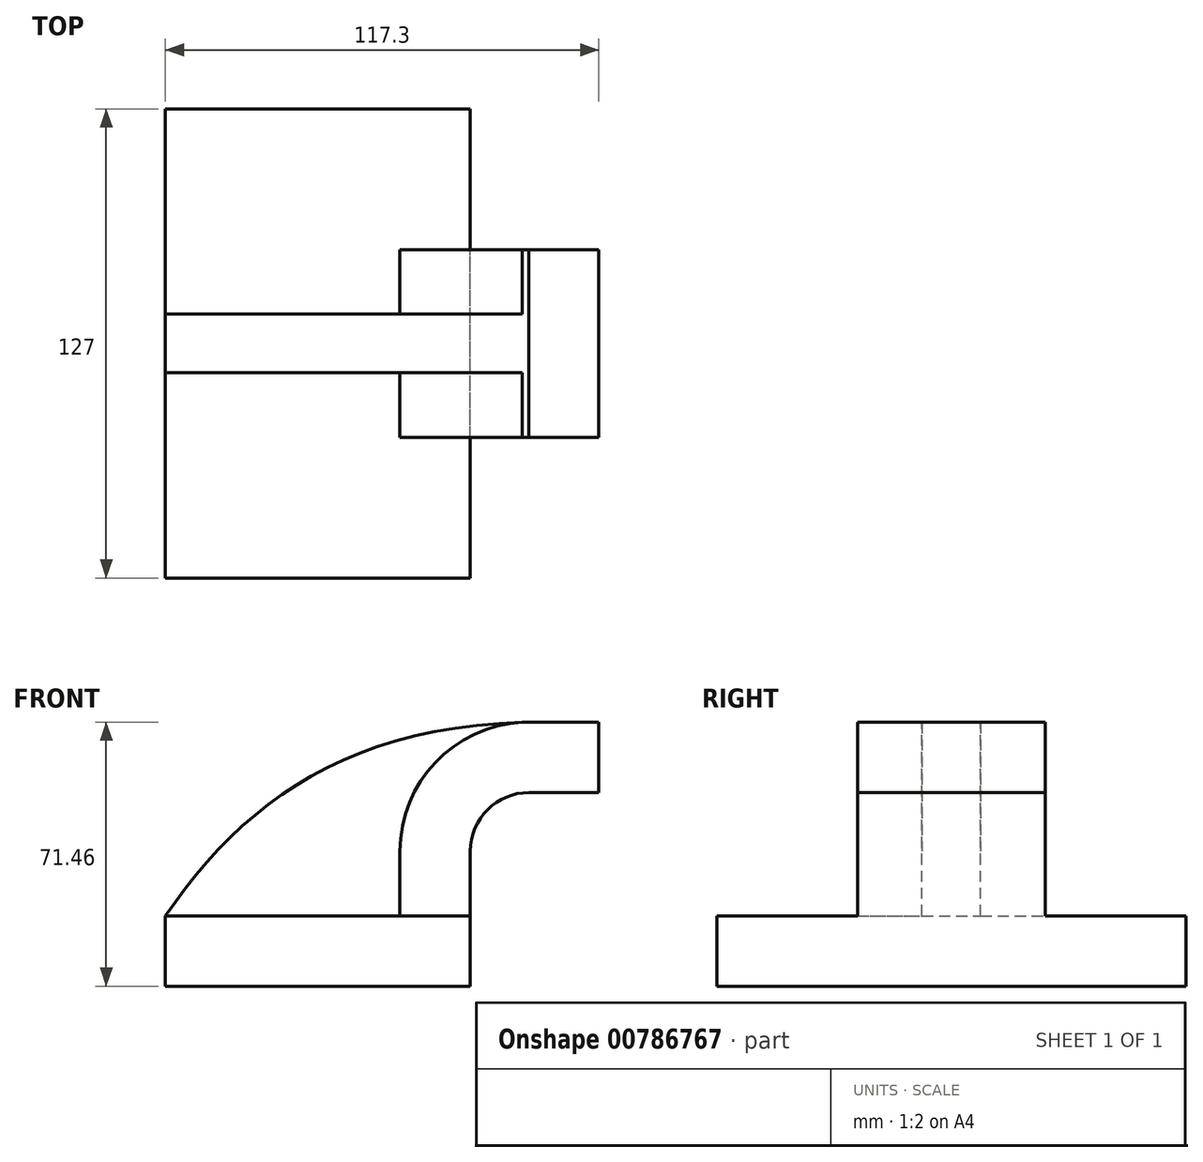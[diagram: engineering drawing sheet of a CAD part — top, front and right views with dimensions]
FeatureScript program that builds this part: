
annotation { "Feature Type Name" : "Feature", "Feature Type Description" : "" }
export const myFeature = defineFeature(function(context is Context, id is Id, definition is map)
    precondition{}
    {
        {
            var Q0;
            Q0=qCreatedBy(makeId("Front.planeOp"),FACE);
            var sketch = newSketch(context, id + "F0", { "sketchPlane" : qUnion([Q0])});
            skLineSegment(sketch, "E0.bottom", {"start": v(41.28, -9.52) * mm, "end": v(-41.28, -9.53) * mm});
            skLineSegment(sketch, "E0.top", {"start": v(41.27, 9.53) * mm, "end": v(-41.28, 9.53) * mm});
            skLineSegment(sketch, "E0.left", {"start": v(41.28, -9.52) * mm, "end": v(41.28, 9.53) * mm});
            skLineSegment(sketch, "E0.right", {"start": v(-41.28, -9.52) * mm, "end": v(-41.28, 9.53) * mm});
            skPoint(sketch, "E0.middle", {"position": v(0, 0) * mm});
            skLineSegment(sketch, "E1.bottom", {"start": v(111.12, 38.1) * mm, "end": v(60.32, 38.1) * mm});
            skLineSegment(sketch, "E1.top", {"start": v(111.12, 66.68) * mm, "end": v(60.32, 66.68) * mm});
            skLineSegment(sketch, "E1.left", {"start": v(60.32, 38.1) * mm, "end": v(60.32, 66.68) * mm});
            skLineSegment(sketch, "E1.right", {"start": v(111.12, 38.1) * mm, "end": v(111.12, 66.68) * mm});
            skPoint(sketch, "E1.middle", {"position": v(85.72, 52.39) * mm});
            skLineSegment(sketch, "E2", {"start": v(41.27, 9.53) * mm, "end": v(41.27, 27) * mm});
            skArc(sketch, "E3", {"start": v(41.27, 27) * mm, "mid": v(45.92, 38.23) * mm, "end": v(57.15, 42.88) * mm});
            skLineSegment(sketch, "E4", {"start": v(57.15, 42.88) * mm, "end": v(76.02, 42.88) * mm});
            skArc(sketch, "E5.0", {"start": v(22.23, 27) * mm, "mid": v(32.45, 51.7) * mm, "end": v(57.15, 61.93) * mm});
            skLineSegment(sketch, "E5.1", {"start": v(22.22, 9.53) * mm, "end": v(22.22, 27) * mm});
            skLineSegment(sketch, "E6", {"start": v(57.15, 61.93) * mm, "end": v(76.02, 61.93) * mm});
            skFitSpline(sketch, "E7", {"points": [v(-41.28, 9.52) * mm, v(57.15, 61.93) * mm], "startDerivative": vector(61.4, 89.44) * mm, "endDerivative": vector(150.97, 3.15) * mm});
            skLineSegment(sketch, "E8", {"start": v(76.02, 66.68) * mm, "end": v(76.02, 38.1) * mm});
            skSolve(sketch);
        }
        {
            var Q0;
            Q0=makeQuery(id+"F0.imprint","IMPRINT",FACE,{"disambiguationData":[TD([[makeQuery(id+"F0.imprint","IMPRINT",EDGE,{"derivedFrom":sQuery(id+"F0.wireOp",EDGE,"E0.bottom")}),-1.0]])]});
            extrude(context, id + "F1", {"entities" : qUnion([Q0]), "endBound" : BoundingType.SYMMETRIC, "depth" : 127 * mm, "offsetDistance" : 25.4 * mm});
        }
        {
            var Q0;
            {var subQ1=sQuery(id+"F0.wireOp",EDGE,"E2");Q0=makeQuery(id+"F0.imprint","IMPRINT",FACE,{"disambiguationData":[TD([[makeQuery(id+"F0.imprint","IMPRINT",EDGE,{"derivedFrom":subQ1}),1.0]])]});}
            var Q1;
            {var subQ0=sQuery(id+"F0.wireOp",EDGE,"E4");var subQ1=sQuery(id+"F0.wireOp",EDGE,"E1.left");var subQ2=makeQuery(id+"F0.imprint","INTERSECT",VERTEX,{"derivedFrom":[subQ1,subQ0]});Q1=makeQuery(id+"F0.imprint","IMPRINT",FACE,{"disambiguationData":[TD([[makeQuery(id+"F0.imprint","IMPRINT",EDGE,{"disambiguationData":[TD([[subQ2,-1.0]])],"derivedFrom":subQ1}),-1.0]])]});}
            extrude(context, id + "F2", {"entities" : qUnion([Q0, Q1]), "operationType" : NewBodyOperationType.ADD, "endBound" : BoundingType.SYMMETRIC, "depth" : 50.8 * mm, "offsetDistance" : 25.4 * mm});
        }
        {
            var Q0;
            {var subQ3=sQuery(id+"F0.wireOp",EDGE,"E5.1");Q0=makeQuery(id+"F0.imprint","IMPRINT",FACE,{"disambiguationData":[TD([[makeQuery(id+"F0.imprint","IMPRINT",EDGE,{"derivedFrom":subQ3}),1.0]])]});}
            extrude(context, id + "F3", {"entities" : qUnion([Q0]), "operationType" : NewBodyOperationType.ADD, "endBound" : BoundingType.SYMMETRIC, "depth" : 15.88 * mm, "offsetDistance" : 25.4 * mm});
        }
    });
